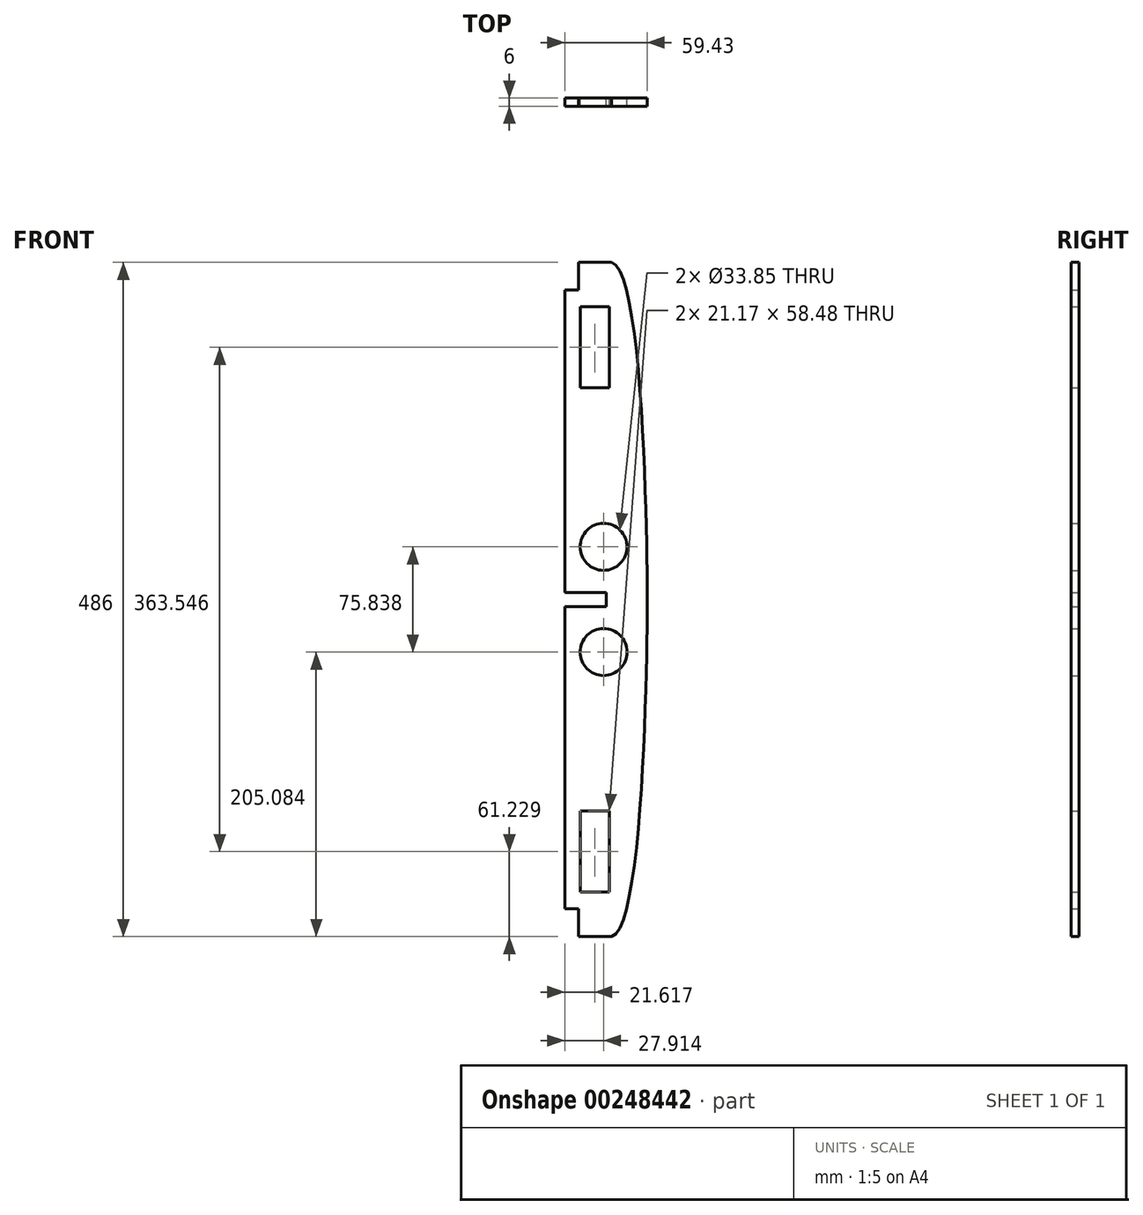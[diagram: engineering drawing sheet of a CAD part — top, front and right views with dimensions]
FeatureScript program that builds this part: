
annotation { "Feature Type Name" : "Feature", "Feature Type Description" : "" }
export const myFeature = defineFeature(function(context is Context, id is Id, definition is map)
    precondition{}
    {
        {
            var Q0;
            Q0=qCreatedBy(makeId("Front.planeOp"),FACE);
            var sketch = newSketch(context, id + "F0", { "sketchPlane" : qUnion([Q0])});
            skLineSegment(sketch, "E0.top", {"start": v(203.9, 162.56) * mm, "end": v(154.46, 162.56) * mm});
            skLineSegment(sketch, "E1", {"start": v(204.46, -80.44) * mm, "end": v(144.46, -80.44) * mm});
            skLineSegment(sketch, "E2", {"start": v(203.9, 162.56) * mm, "end": v(203.9, -81.33) * mm});
            skLineSegment(sketch, "E3.bottom", {"start": v(176.66, 130.58) * mm, "end": v(155.5, 130.58) * mm});
            skLineSegment(sketch, "E3.top", {"start": v(176.66, 72.1) * mm, "end": v(155.5, 72.1) * mm});
            skLineSegment(sketch, "E3.left", {"start": v(176.66, 130.58) * mm, "end": v(176.66, 72.1) * mm});
            skLineSegment(sketch, "E3.right", {"start": v(155.5, 130.58) * mm, "end": v(155.5, 72.1) * mm});
            skCircle(sketch, "E4", {"center": v(172.37, -42.52) * mm, "radius": 16.93 * mm});
            skLineSegment(sketch, "E5", {"start": v(203.9, -80.44) * mm, "end": v(204.46, -80.44) * mm});
            skFitSpline(sketch, "E6", {"points": [v(178.3, 162.56) * mm, v(203.9, -80.44) * mm], "startDerivative": vector(76.9, -21.6) * mm, "endDerivative": vector(-0.1, 2.67) * mm});
            skLineSegment(sketch, "E7.MirrorCS", {"start": v(176.66, -291.45) * mm, "end": v(176.66, -232.97) * mm});
            skCircle(sketch, "E8.MirrorC", {"center": v(172.37, -118.36) * mm, "radius": 16.93 * mm});
            skLineSegment(sketch, "E9.MirrorCS", {"start": v(176.66, -291.45) * mm, "end": v(155.5, -291.45) * mm});
            skLineSegment(sketch, "E10.MirrorCS", {"start": v(155.5, -291.45) * mm, "end": v(155.5, -232.97) * mm});
            skLineSegment(sketch, "E11.MirrorCS", {"start": v(176.66, -232.97) * mm, "end": v(155.5, -232.97) * mm});
            skLineSegment(sketch, "E12.MirrorCS", {"start": v(203.9, -323.44) * mm, "end": v(203.9, -79.55) * mm});
            skFitSpline(sketch, "E13.MirrorCS", {"points": [v(178.3, -323.44) * mm, v(203.9, -80.44) * mm], "startDerivative": vector(76.9, 21.6) * mm, "endDerivative": vector(-0.1, -2.67) * mm});
            skLineSegment(sketch, "E14.MirrorCS", {"start": v(203.9, -323.44) * mm, "end": v(154.46, -323.44) * mm});
            skLineSegment(sketch, "E15", {"start": v(174.46, -80.44) * mm, "end": v(174.46, -75.44) * mm});
            skLineSegment(sketch, "E16", {"start": v(174.46, -80.44) * mm, "end": v(174.46, -85.44) * mm});
            skLineSegment(sketch, "E17", {"start": v(174.46, -75.44) * mm, "end": v(144.46, -75.44) * mm});
            skLineSegment(sketch, "E18", {"start": v(174.46, -85.44) * mm, "end": v(144.46, -85.44) * mm});
            skLineSegment(sketch, "E19", {"start": v(154.46, 162.56) * mm, "end": v(154.46, 142.56) * mm});
            skLineSegment(sketch, "E20", {"start": v(154.46, 142.56) * mm, "end": v(144.46, 142.56) * mm});
            skLineSegment(sketch, "E21", {"start": v(154.46, 162.56) * mm, "end": v(178.46, 162.56) * mm});
            skLineSegment(sketch, "E22", {"start": v(144.46, 142.56) * mm, "end": v(144.46, -80.44) * mm});
            skLineSegment(sketch, "E23.MirrorCS", {"start": v(154.46, -323.44) * mm, "end": v(154.46, -303.44) * mm});
            skLineSegment(sketch, "E24.MirrorCS", {"start": v(154.46, -303.44) * mm, "end": v(144.46, -303.44) * mm});
            skLineSegment(sketch, "E25", {"start": v(144.46, -303.44) * mm, "end": v(144.46, -80.44) * mm});
            skLineSegment(sketch, "E26", {"start": v(154.46, -323.44) * mm, "end": v(178.46, -323.44) * mm});
            skSolve(sketch);
        }
        {
            var Q0;
            Q0=makeQuery(id+"F0.imprint","IMPRINT",FACE,{"disambiguationData":[TD([[makeQuery(id+"F0.imprint","IMPRINT",EDGE,{"derivedFrom":sQuery(id+"F0.wireOp",EDGE,"E7.MirrorCS")}),-1.0]])]});
            var Q1;
            Q1=makeQuery(id+"F0.imprint","IMPRINT",FACE,{"disambiguationData":[TD([[makeQuery(id+"F0.imprint","IMPRINT",EDGE,{"derivedFrom":sQuery(id+"F0.wireOp",EDGE,"E3.bottom")}),-1.0]])]});
            extrude(context, id + "F1", {"entities" : qUnion([Q0, Q1]), "depth" : 6 * mm});
        }
    });
